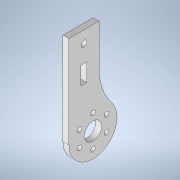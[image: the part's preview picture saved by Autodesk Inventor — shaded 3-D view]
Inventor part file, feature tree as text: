
AUTODESK INVENTOR PART (.ipt)
format: ipt  version: 2022 (Build 260153000, 153)  size: 150,016 bytes
history: native  units: mm
features: extrude x1, sketch x1
ambient origin geometry x8: Origin, YZ Plane, XZ Plane, XY Plane, X Axis, Y Axis, Z Axis, Center Point
bodies: Solid1 (feature_tree)
feature tree (2):
  extrude  "Extrusion1"  Depth=3.0mm
  sketch  "Sketch1"  dims[d1=60.0mm d2=24.0mm d3=8.75mm d4=18.0mm d5=1.2mm d7=360.0deg d8=45.0mm d12=12.0mm d15=58.0mm d16=15.0mm d18=30.0mm d19=3.0mm d20=0.0mm d22=3.0mm d23=6.0mm d28=7.5mm d29=15.0mm d31=9.0mm d32=3.0mm d30=0.5mm]
